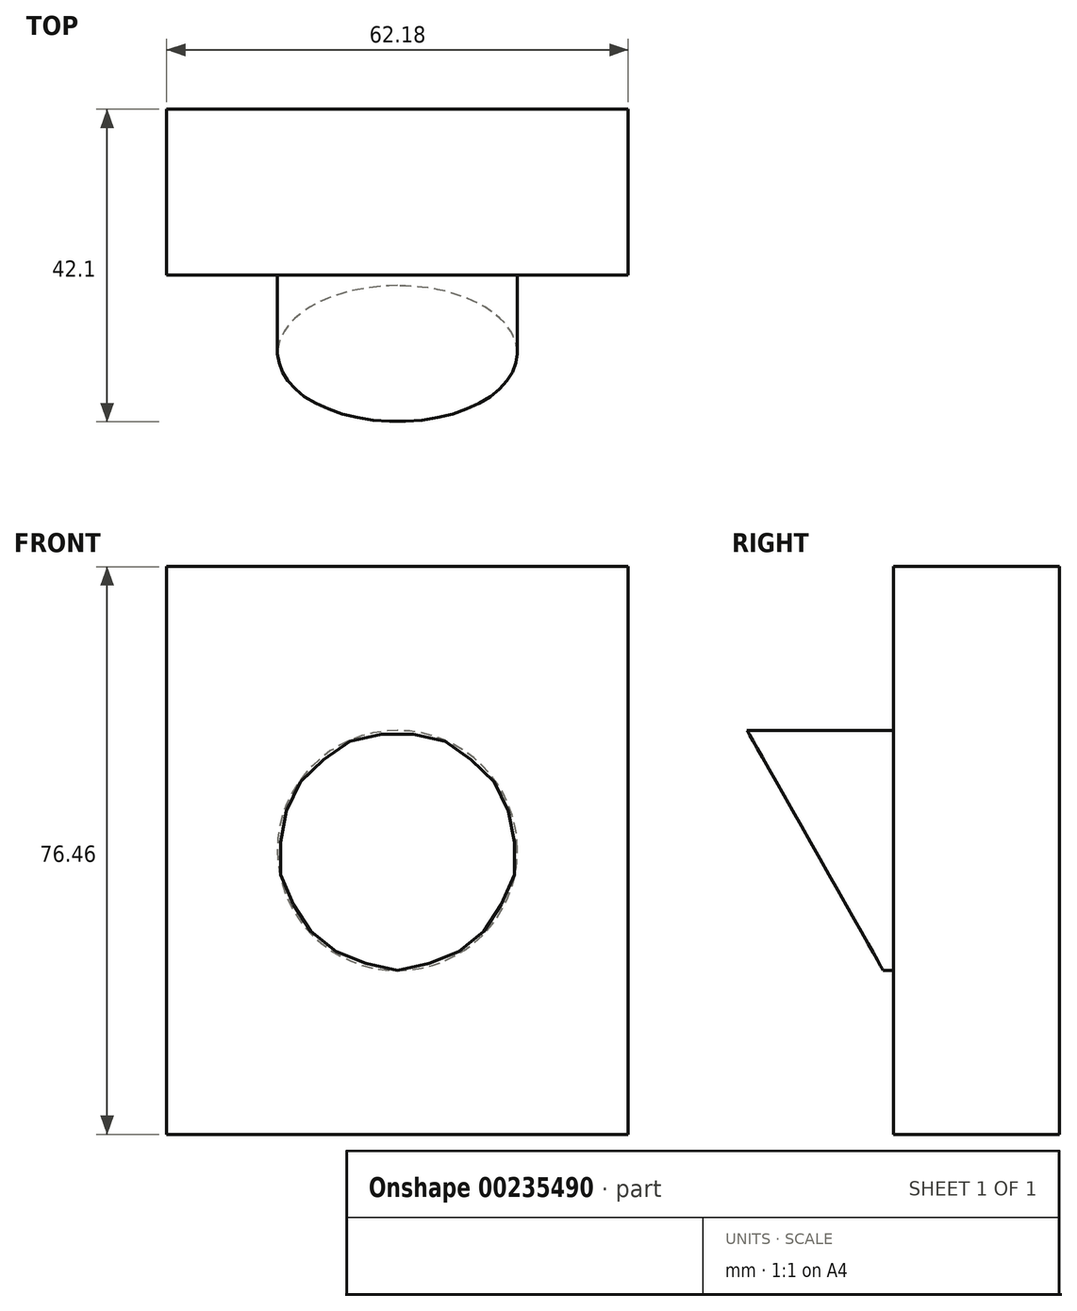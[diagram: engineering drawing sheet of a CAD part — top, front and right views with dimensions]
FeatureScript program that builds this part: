
annotation { "Feature Type Name" : "Feature", "Feature Type Description" : "" }
export const myFeature = defineFeature(function(context is Context, id is Id, definition is map)
    precondition{}
    {
        {
            var Q0;
            Q0=qCreatedBy(makeId("Front.planeOp"),FACE);
            var sketch = newSketch(context, id + "F0", { "sketchPlane" : qUnion([Q0])});
            skLineSegment(sketch, "E0.bottom", {"start": v(31.09, 38.23) * mm, "end": v(-31.09, 38.23) * mm});
            skLineSegment(sketch, "E0.top", {"start": v(31.09, -38.23) * mm, "end": v(-31.09, -38.23) * mm});
            skLineSegment(sketch, "E0.left", {"start": v(31.09, 38.23) * mm, "end": v(31.09, -38.23) * mm});
            skLineSegment(sketch, "E0.right", {"start": v(-31.09, 38.23) * mm, "end": v(-31.09, -38.23) * mm});
            skPoint(sketch, "E0.middle", {"position": v(0, 0) * mm});
            skCircle(sketch, "E1", {"center": v(0, 0) * mm, "radius": 16.17 * mm});
            skSolve(sketch);
        }
        {
            var Q0;
            Q0=makeQuery(id+"F0.imprint","IMPRINT",FACE,{"disambiguationData":[TD([[makeQuery(id+"F0.imprint","IMPRINT",EDGE,{"derivedFrom":sQuery(id+"F0.wireOp",EDGE,"E1")}),1.0]])]});
            var Q1;
            Q1=makeQuery(id+"F0.imprint","IMPRINT",FACE,{"disambiguationData":[TD([[makeQuery(id+"F0.imprint","IMPRINT",EDGE,{"derivedFrom":sQuery(id+"F0.wireOp",EDGE,"E0.bottom")}),1.0]])]});
            extrude(context, id + "F1", {"entities" : qUnion([Q0, Q1]), "depth" : 22.35 * mm});
        }
        {
            var Q0;
            Q0=makeQuery(id+"F0.imprint","IMPRINT",FACE,{"disambiguationData":[TD([[makeQuery(id+"F0.imprint","IMPRINT",EDGE,{"derivedFrom":sQuery(id+"F0.wireOp",EDGE,"E1")}),1.0]])]});
            extrude(context, id + "F2", {"entities" : qUnion([Q0]), "operationType" : NewBodyOperationType.ADD, "depth" : 43.18 * mm});
        }
        {
            var Q0;
            Q0=qCreatedBy(makeId("Right.planeOp"),FACE);
            var sketch = newSketch(context, id + "F3", { "sketchPlane" : qUnion([Q0])});
            skLineSegment(sketch, "E2.bottom", {"start": v(-58.44, 18.22) * mm, "end": v(-43.02, 17.78) * mm});
            skLineSegment(sketch, "E2.top", {"start": v(-58.44, -16.7) * mm, "end": v(-23.45, -16.7) * mm});
            skLineSegment(sketch, "E2.left", {"start": v(-58.44, 18.22) * mm, "end": v(-58.44, -16.7) * mm});
            skLineSegment(sketch, "E2.right", {"start": v(-43.02, 17.78) * mm, "end": v(-23.45, -16.7) * mm});
            skSolve(sketch);
        }
        {
            var Q0;
            Q0=makeQuery(id+"F3.imprint","IMPRINT",FACE,{"disambiguationData":[TD([[makeQuery(id+"F3.imprint","IMPRINT",EDGE,{"derivedFrom":sQuery(id+"F3.wireOp",EDGE,"E2.bottom")}),-1.0]])]});
            extrude(context, id + "F4", {"entities" : qUnion([Q0]), "operationType" : NewBodyOperationType.REMOVE, "depth" : 25.4 * mm});
        }
        {
            var Q0;
            Q0 = qSketchRegion(id + "F3", true);
            extrude(context, id + "F5", {"entities" : qUnion([Q0]), "operationType" : NewBodyOperationType.REMOVE, "oppositeDirection" : true, "depth" : 25.4 * mm});
        }
    });
